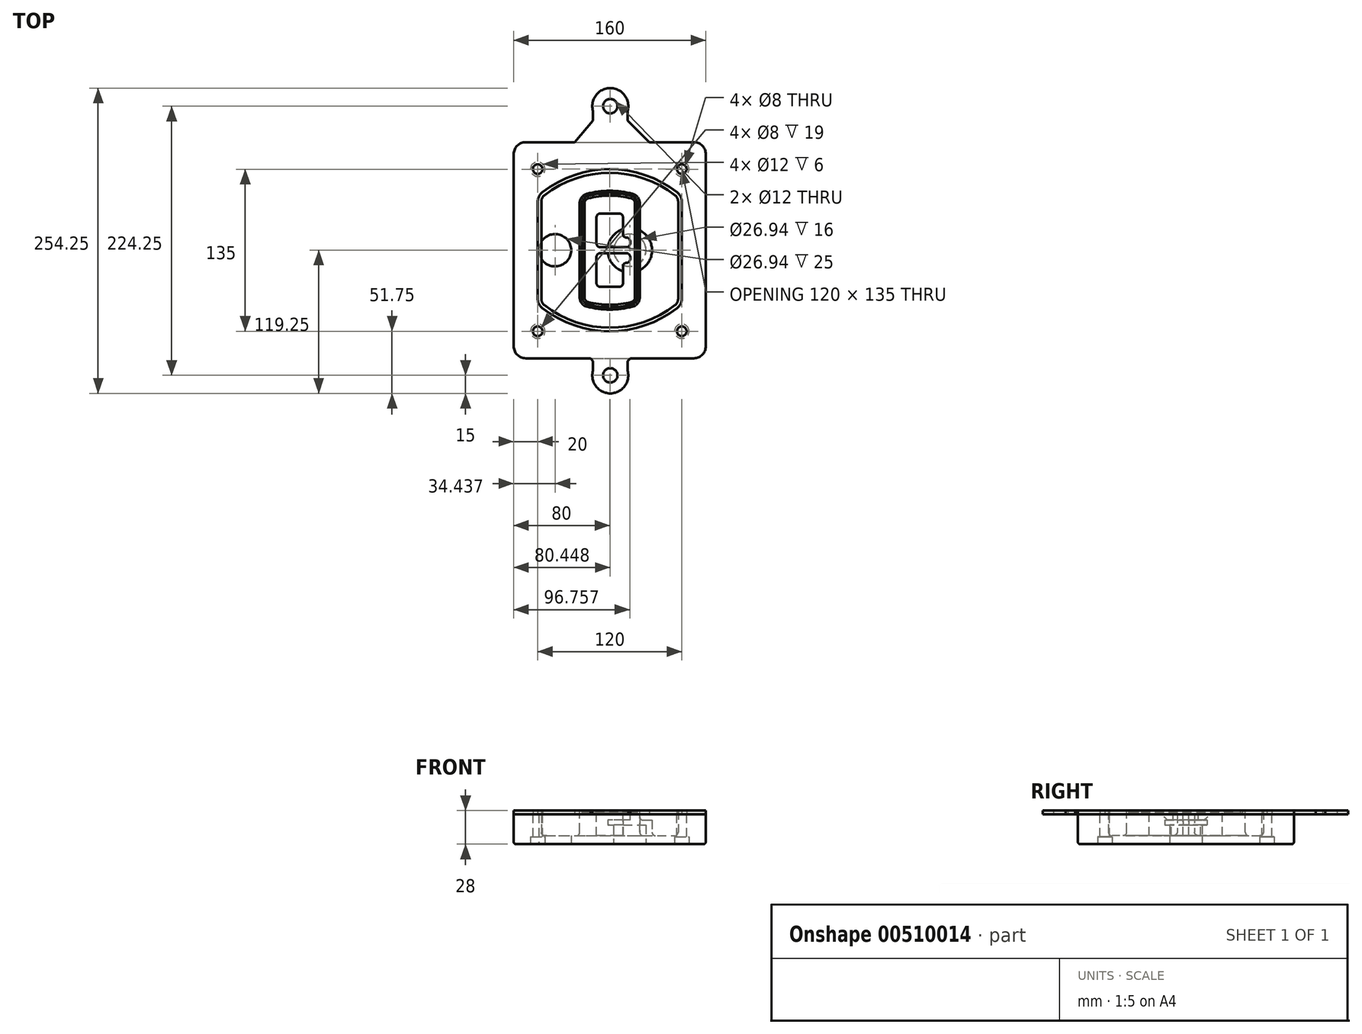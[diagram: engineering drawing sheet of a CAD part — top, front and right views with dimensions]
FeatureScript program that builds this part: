
annotation { "Feature Type Name" : "Feature", "Feature Type Description" : "" }
export const myFeature = defineFeature(function(context is Context, id is Id, definition is map)
    precondition{}
    {
        {
            var Q0;
            Q0=qCreatedBy(makeId("Top.planeOp"),FACE);
            var sketch = newSketch(context, id + "F0", { "sketchPlane" : qUnion([Q0])});
            skPoint(sketch, "E0.rect.middle", {"position": v(0, 0) * mm});
            skLineSegment(sketch, "E1.bottom", {"start": v(-70, -90) * mm, "end": v(70, -90) * mm});
            skLineSegment(sketch, "E1.top", {"start": v(-70, 90) * mm, "end": v(70, 90) * mm});
            skLineSegment(sketch, "E1.left", {"start": v(-80, -80) * mm, "end": v(-80, 80) * mm});
            skLineSegment(sketch, "E1.right", {"start": v(80, -80) * mm, "end": v(80, 80) * mm});
            skLineSegment(sketch, "E2", {"start": v(-80, 90) * mm, "end": v(80, -90) * mm, "construction": true});
            skLineSegment(sketch, "E3", {"start": v(80, 90) * mm, "end": v(-80, -90) * mm, "construction": true});
            skCircle(sketch, "E4", {"center": v(-60, 67.5) * mm, "radius": 4 * mm});
            skCircle(sketch, "E5", {"center": v(60, 67.5) * mm, "radius": 4 * mm});
            skCircle(sketch, "E6", {"center": v(60, -67.5) * mm, "radius": 4 * mm});
            skCircle(sketch, "E7", {"center": v(-60, -67.5) * mm, "radius": 4 * mm});
            skLineSegment(sketch, "E8", {"start": v(-60, 67.5) * mm, "end": v(60, 67.5) * mm, "construction": true});
            skLineSegment(sketch, "E9", {"start": v(60, 67.5) * mm, "end": v(60, -67.5) * mm, "construction": true});
            skLineSegment(sketch, "E10", {"start": v(60, -67.5) * mm, "end": v(-60, -67.5) * mm, "construction": true});
            skLineSegment(sketch, "E11", {"start": v(-60, -67.5) * mm, "end": v(-60, 67.5) * mm, "construction": true});
            skLineSegment(sketch, "E12", {"start": v(-60, 40.3) * mm, "end": v(-60, -40.3) * mm});
            skLineSegment(sketch, "E13", {"start": v(60, 40.3) * mm, "end": v(60, -40.3) * mm});
            skArc(sketch, "E14", {"start": v(56.15, 48.18) * mm, "mid": v(0, 67.5) * mm, "end": v(-56.15, 48.18) * mm});
            skArc(sketch, "E15", {"start": v(-56.15, -48.18) * mm, "mid": v(0, -67.5) * mm, "end": v(56.15, -48.18) * mm});
            skLineSegment(sketch, "E16", {"start": v(-60, 0) * mm, "end": v(60, 0) * mm, "construction": true});
            skPoint(sketch, "E17.visualSharp", {"position": v(-60, -45) * mm});
            skArc(sketch, "E17.filletArc", {"start": v(-60, -40.3) * mm, "mid": v(-58.99, -44.68) * mm, "end": v(-56.15, -48.18) * mm});
            skPoint(sketch, "E18.visualSharp", {"position": v(-60, 45) * mm});
            skArc(sketch, "E18.filletArc", {"start": v(-56.15, 48.18) * mm, "mid": v(-58.99, 44.68) * mm, "end": v(-60, 40.3) * mm});
            skPoint(sketch, "E19.visualSharp", {"position": v(60, 45) * mm});
            skArc(sketch, "E19.filletArc", {"start": v(60, 40.3) * mm, "mid": v(58.99, 44.68) * mm, "end": v(56.15, 48.18) * mm});
            skPoint(sketch, "E20.visualSharp", {"position": v(60, -45) * mm});
            skArc(sketch, "E20.filletArc", {"start": v(56.15, -48.18) * mm, "mid": v(58.99, -44.68) * mm, "end": v(60, -40.3) * mm});
            skPoint(sketch, "E21.visualSharp", {"position": v(-80, 90) * mm});
            skArc(sketch, "E21.filletArc", {"start": v(-70, 90) * mm, "mid": v(-77.07, 87.07) * mm, "end": v(-80, 80) * mm});
            skPoint(sketch, "E22.visualSharp", {"position": v(80, 90) * mm});
            skArc(sketch, "E22.filletArc", {"start": v(80, 80) * mm, "mid": v(77.07, 87.07) * mm, "end": v(70, 90) * mm});
            skPoint(sketch, "E23.visualSharp", {"position": v(80, -90) * mm});
            skArc(sketch, "E23.filletArc", {"start": v(70, -90) * mm, "mid": v(77.07, -87.07) * mm, "end": v(80, -80) * mm});
            skPoint(sketch, "E24.visualSharp", {"position": v(-80, -90) * mm});
            skArc(sketch, "E24.filletArc", {"start": v(-80, -80) * mm, "mid": v(-77.07, -87.07) * mm, "end": v(-70, -90) * mm});
            skArc(sketch, "E25.0", {"start": v(57, 40.3) * mm, "mid": v(56.3, 43.36) * mm, "end": v(54.3, 45.81) * mm});
            skLineSegment(sketch, "E25.1", {"start": v(57, 40.3) * mm, "end": v(57, -40.3) * mm});
            skArc(sketch, "E25.2", {"start": v(54.3, -45.81) * mm, "mid": v(56.3, -43.36) * mm, "end": v(57, -40.3) * mm});
            skArc(sketch, "E25.3", {"start": v(-54.3, -45.81) * mm, "mid": v(0, -64.5) * mm, "end": v(54.3, -45.81) * mm});
            skArc(sketch, "E25.4", {"start": v(-57, -40.3) * mm, "mid": v(-56.3, -43.36) * mm, "end": v(-54.3, -45.81) * mm});
            skArc(sketch, "E25.5", {"start": v(54.3, 45.81) * mm, "mid": v(0, 64.5) * mm, "end": v(-54.3, 45.81) * mm});
            skLineSegment(sketch, "E25.6", {"start": v(-57, 40.3) * mm, "end": v(-57, -40.3) * mm});
            skArc(sketch, "E25.7", {"start": v(-54.3, 45.81) * mm, "mid": v(-56.3, 43.36) * mm, "end": v(-57, 40.3) * mm});
            skArc(sketch, "E26.0", {"start": v(-58.62, 51.33) * mm, "mid": v(-62.58, 46.43) * mm, "end": v(-64, 40.3) * mm});
            skArc(sketch, "E26.1", {"start": v(58.62, 51.33) * mm, "mid": v(0, 71.5) * mm, "end": v(-58.62, 51.33) * mm});
            skArc(sketch, "E26.2", {"start": v(64, 40.3) * mm, "mid": v(62.58, 46.43) * mm, "end": v(58.62, 51.33) * mm});
            skLineSegment(sketch, "E26.3", {"start": v(64, 40.3) * mm, "end": v(64, -40.3) * mm});
            skArc(sketch, "E26.4", {"start": v(58.62, -51.33) * mm, "mid": v(62.58, -46.43) * mm, "end": v(64, -40.3) * mm});
            skLineSegment(sketch, "E26.5", {"start": v(-64, 40.3) * mm, "end": v(-64, -40.3) * mm});
            skArc(sketch, "E26.6", {"start": v(-58.62, -51.33) * mm, "mid": v(0, -71.5) * mm, "end": v(58.62, -51.33) * mm});
            skArc(sketch, "E26.7", {"start": v(-64, -40.3) * mm, "mid": v(-62.58, -46.43) * mm, "end": v(-58.62, -51.33) * mm});
            skSolve(sketch);
        }
        {
            var Q0;
            Q0=makeQuery(id+"F0.imprint","IMPRINT",FACE,{"disambiguationData":[TD([[makeQuery(id+"F0.imprint","IMPRINT",EDGE,{"derivedFrom":sQuery(id+"F0.wireOp",EDGE,"E1.bottom")}),1.0]])]});
            var Q1;
            Q1=makeQuery(id+"F0.imprint","IMPRINT",FACE,{"disambiguationData":[TD([[makeQuery(id+"F0.imprint","IMPRINT",EDGE,{"derivedFrom":sQuery(id+"F0.wireOp",EDGE,"E12")}),1.0]])]});
            var Q2;
            Q2=makeQuery(id+"F0.imprint","IMPRINT",FACE,{"disambiguationData":[TD([[makeQuery(id+"F0.imprint","IMPRINT",EDGE,{"derivedFrom":sQuery(id+"F0.wireOp",EDGE,"E25.0")}),1.0]])]});
            var Q3;
            Q3=makeQuery(id+"F0.imprint","IMPRINT",FACE,{"disambiguationData":[TD([[makeQuery(id+"F0.imprint","IMPRINT",EDGE,{"derivedFrom":sQuery(id+"F0.wireOp",EDGE,"E12")}),-1.0]])]});
            extrude(context, id + "F1", {"entities" : qUnion([Q0, Q1, Q2, Q3]), "oppositeDirection" : true, "depth" : 25 * mm});
        }
        {
            var Q0;
            Q0=makeQuery(id+"F0.imprint","IMPRINT",FACE,{"disambiguationData":[TD([[makeQuery(id+"F0.imprint","IMPRINT",EDGE,{"derivedFrom":sQuery(id+"F0.wireOp",EDGE,"E12")}),1.0]])]});
            extrude(context, id + "F2", {"entities" : qUnion([Q0]), "operationType" : NewBodyOperationType.ADD, "depth" : 3 * mm});
        }
        {
            var Q0;
            Q0=makeQuery(id+"F0.imprint","IMPRINT",FACE,{"disambiguationData":[TD([[makeQuery(id+"F0.imprint","IMPRINT",EDGE,{"derivedFrom":sQuery(id+"F0.wireOp",EDGE,"E25.0")}),1.0]])]});
            extrude(context, id + "F3", {"entities" : qUnion([Q0]), "operationType" : NewBodyOperationType.REMOVE, "oppositeDirection" : true, "depth" : 18 * mm});
        }
        {
            var Q0;
            Q0=makeQuery(id+"F2.opExtrude","CAP_FACE",FACE,{"disambiguationData":[OSD([sQuery(id+"F0.wireOp",EDGE,"E12"),sQuery(id+"F0.wireOp",EDGE,"E13"),sQuery(id+"F0.wireOp",EDGE,"E14"),sQuery(id+"F0.wireOp",EDGE,"E15"),sQuery(id+"F0.wireOp",EDGE,"E17.filletArc"),sQuery(id+"F0.wireOp",EDGE,"E18.filletArc"),sQuery(id+"F0.wireOp",EDGE,"E19.filletArc"),sQuery(id+"F0.wireOp",EDGE,"E20.filletArc"),sQuery(id+"F0.wireOp",EDGE,"E25.0"),sQuery(id+"F0.wireOp",EDGE,"E25.1"),sQuery(id+"F0.wireOp",EDGE,"E25.2"),sQuery(id+"F0.wireOp",EDGE,"E25.3"),sQuery(id+"F0.wireOp",EDGE,"E25.4"),sQuery(id+"F0.wireOp",EDGE,"E25.5"),sQuery(id+"F0.wireOp",EDGE,"E25.6"),sQuery(id+"F0.wireOp",EDGE,"E25.7")])],"isStart":false});
            var sketch = newSketch(context, id + "F4", { "sketchPlane" : qUnion([Q0])});
            skArc(sketch, "E27.0", {"start": v(-19.08, -46.97) * mm, "mid": v(0, -49.5) * mm, "end": v(19.08, -46.97) * mm});
            skArc(sketch, "E28.0", {"start": v(19.08, 46.97) * mm, "mid": v(0, 49.5) * mm, "end": v(-19.08, 46.97) * mm});
            skLineSegment(sketch, "E29", {"start": v(-25, 39.25) * mm, "end": v(-25, -39.25) * mm});
            skLineSegment(sketch, "E30", {"start": v(25, 39.25) * mm, "end": v(25, -39.25) * mm});
            skLineSegment(sketch, "E31", {"start": v(-25, 45.1) * mm, "end": v(25, 45.1) * mm, "construction": true});
            skLineSegment(sketch, "E32", {"start": v(-25, -45.1) * mm, "end": v(25, -45.1) * mm, "construction": true});
            skPoint(sketch, "E33.visualSharp", {"position": v(-25, 45.1) * mm});
            skArc(sketch, "E33.filletArc", {"start": v(-19.08, 46.97) * mm, "mid": v(-23.35, 44.11) * mm, "end": v(-25, 39.25) * mm});
            skPoint(sketch, "E34.visualSharp", {"position": v(25, 45.1) * mm});
            skArc(sketch, "E34.filletArc", {"start": v(25, 39.25) * mm, "mid": v(23.35, 44.11) * mm, "end": v(19.08, 46.97) * mm});
            skPoint(sketch, "E35.visualSharp", {"position": v(25, -45.1) * mm});
            skArc(sketch, "E35.filletArc", {"start": v(19.08, -46.97) * mm, "mid": v(23.35, -44.11) * mm, "end": v(25, -39.25) * mm});
            skPoint(sketch, "E36.visualSharp", {"position": v(-25, -45.1) * mm});
            skArc(sketch, "E36.filletArc", {"start": v(-25, -39.25) * mm, "mid": v(-23.35, -44.11) * mm, "end": v(-19.08, -46.97) * mm});
            skArc(sketch, "E37.0", {"start": v(54.3, 45.81) * mm, "mid": v(0, 64.5) * mm, "end": v(-54.3, 45.81) * mm});
            skArc(sketch, "E37.1", {"start": v(-54.3, 45.81) * mm, "mid": v(-56.3, 43.36) * mm, "end": v(-57, 40.3) * mm});
            skLineSegment(sketch, "E37.2", {"start": v(-57, 40.3) * mm, "end": v(-57, -40.3) * mm});
            skArc(sketch, "E37.3", {"start": v(-57, -40.3) * mm, "mid": v(-56.3, -43.36) * mm, "end": v(-54.3, -45.81) * mm});
            skArc(sketch, "E37.4", {"start": v(-54.3, -45.81) * mm, "mid": v(0, -64.5) * mm, "end": v(54.3, -45.81) * mm});
            skArc(sketch, "E37.5", {"start": v(54.3, -45.81) * mm, "mid": v(56.3, -43.36) * mm, "end": v(57, -40.3) * mm});
            skLineSegment(sketch, "E37.6", {"start": v(57, 40.3) * mm, "end": v(57, -40.3) * mm});
            skArc(sketch, "E37.7", {"start": v(57, 40.3) * mm, "mid": v(56.3, 43.36) * mm, "end": v(54.3, 45.81) * mm});
            skLineSegment(sketch, "E38.0", {"start": v(23, 39.25) * mm, "end": v(23, -39.25) * mm});
            skArc(sketch, "E38.1", {"start": v(18.56, -45.04) * mm, "mid": v(21.76, -42.9) * mm, "end": v(23, -39.25) * mm});
            skArc(sketch, "E38.2", {"start": v(-18.56, -45.04) * mm, "mid": v(0, -47.5) * mm, "end": v(18.56, -45.04) * mm});
            skArc(sketch, "E38.3", {"start": v(-23, -39.25) * mm, "mid": v(-21.76, -42.9) * mm, "end": v(-18.56, -45.04) * mm});
            skLineSegment(sketch, "E38.4", {"start": v(-23, 39.25) * mm, "end": v(-23, -39.25) * mm});
            skArc(sketch, "E38.5", {"start": v(23, 39.25) * mm, "mid": v(21.76, 42.9) * mm, "end": v(18.56, 45.04) * mm});
            skArc(sketch, "E38.6", {"start": v(-18.56, 45.04) * mm, "mid": v(-21.76, 42.9) * mm, "end": v(-23, 39.25) * mm});
            skArc(sketch, "E38.7", {"start": v(18.56, 45.04) * mm, "mid": v(0, 47.5) * mm, "end": v(-18.56, 45.04) * mm});
            skArc(sketch, "E39.0", {"start": v(21, 39.25) * mm, "mid": v(20.18, 41.68) * mm, "end": v(18.04, 43.1) * mm});
            skLineSegment(sketch, "E39.1", {"start": v(21, 39.25) * mm, "end": v(21, -39.25) * mm});
            skArc(sketch, "E39.2", {"start": v(18.04, -43.1) * mm, "mid": v(20.18, -41.68) * mm, "end": v(21, -39.25) * mm});
            skArc(sketch, "E39.3", {"start": v(-18.04, -43.1) * mm, "mid": v(0, -45.5) * mm, "end": v(18.04, -43.1) * mm});
            skArc(sketch, "E39.4", {"start": v(-21, -39.25) * mm, "mid": v(-20.18, -41.68) * mm, "end": v(-18.04, -43.1) * mm});
            skArc(sketch, "E39.5", {"start": v(18.04, 43.1) * mm, "mid": v(0, 45.5) * mm, "end": v(-18.04, 43.1) * mm});
            skLineSegment(sketch, "E39.6", {"start": v(-21, 39.25) * mm, "end": v(-21, -39.25) * mm});
            skArc(sketch, "E39.7", {"start": v(-18.04, 43.1) * mm, "mid": v(-20.18, 41.68) * mm, "end": v(-21, 39.25) * mm});
            skLineSegment(sketch, "E40", {"start": v(-25, 0) * mm, "end": v(25, 0) * mm, "construction": true});
            skLineSegment(sketch, "E41", {"start": v(-11, 5.5) * mm, "end": v(-11, 27.5) * mm});
            skLineSegment(sketch, "E42", {"start": v(-8, 30.5) * mm, "end": v(8, 30.5) * mm});
            skLineSegment(sketch, "E43", {"start": v(11, 27.5) * mm, "end": v(11, 13.5) * mm});
            skLineSegment(sketch, "E44", {"start": v(14, 10.5) * mm, "end": v(14, 10.5) * mm});
            skLineSegment(sketch, "E45", {"start": v(17, 7.5) * mm, "end": v(17, 5.5) * mm});
            skLineSegment(sketch, "E46", {"start": v(14, 2.5) * mm, "end": v(-8, 2.5) * mm});
            skPoint(sketch, "E47.visualSharp", {"position": v(-11, 30.5) * mm});
            skArc(sketch, "E47.filletArc", {"start": v(-8, 30.5) * mm, "mid": v(-10.12, 29.62) * mm, "end": v(-11, 27.5) * mm});
            skPoint(sketch, "E48.visualSharp", {"position": v(11, 30.5) * mm});
            skArc(sketch, "E48.filletArc", {"start": v(11, 27.5) * mm, "mid": v(10.12, 29.62) * mm, "end": v(8, 30.5) * mm});
            skPoint(sketch, "E49.visualSharp", {"position": v(11, 10.5) * mm});
            skArc(sketch, "E49.filletArc", {"start": v(11, 13.5) * mm, "mid": v(11.88, 11.38) * mm, "end": v(14, 10.5) * mm});
            skPoint(sketch, "E50.visualSharp", {"position": v(17, 10.5) * mm});
            skArc(sketch, "E50.filletArc", {"start": v(17, 7.5) * mm, "mid": v(16.12, 9.62) * mm, "end": v(14, 10.5) * mm});
            skPoint(sketch, "E51.visualSharp", {"position": v(17, 2.5) * mm});
            skArc(sketch, "E51.filletArc", {"start": v(14, 2.5) * mm, "mid": v(16.12, 3.38) * mm, "end": v(17, 5.5) * mm});
            skPoint(sketch, "E52.visualSharp", {"position": v(-11, 2.5) * mm});
            skArc(sketch, "E52.filletArc", {"start": v(-11, 5.5) * mm, "mid": v(-10.12, 3.38) * mm, "end": v(-8, 2.5) * mm});
            skLineSegment(sketch, "E53.0.MirrorCS", {"start": v(14, -2.5) * mm, "end": v(-8, -2.5) * mm});
            skArc(sketch, "E54.0.MirrorCS", {"start": v(-11, -5.5) * mm, "mid": v(-10.12, -3.38) * mm, "end": v(-8, -2.5) * mm});
            skLineSegment(sketch, "E55.0.MirrorCS", {"start": v(-11, -5.5) * mm, "end": v(-11, -27.5) * mm});
            skArc(sketch, "E56.0.MirrorCS", {"start": v(-8, -30.5) * mm, "mid": v(-10.12, -29.62) * mm, "end": v(-11, -27.5) * mm});
            skLineSegment(sketch, "E57.0.MirrorCS", {"start": v(-8, -30.5) * mm, "end": v(8, -30.5) * mm});
            skArc(sketch, "E58.0.MirrorCS", {"start": v(11, -27.5) * mm, "mid": v(10.12, -29.62) * mm, "end": v(8, -30.5) * mm});
            skLineSegment(sketch, "E59.0.MirrorCS", {"start": v(11, -27.5) * mm, "end": v(11, -13.5) * mm});
            skArc(sketch, "E60.0.MirrorCS", {"start": v(11, -13.5) * mm, "mid": v(11.88, -11.38) * mm, "end": v(14, -10.5) * mm});
            skArc(sketch, "E61.0.MirrorCS", {"start": v(17, -7.5) * mm, "mid": v(16.12, -9.62) * mm, "end": v(14, -10.5) * mm});
            skLineSegment(sketch, "E62.0.MirrorCS", {"start": v(17, -7.5) * mm, "end": v(17, -5.5) * mm});
            skArc(sketch, "E63.0.MirrorCS", {"start": v(14, -2.5) * mm, "mid": v(16.12, -3.38) * mm, "end": v(17, -5.5) * mm});
            skSolve(sketch);
        }
        {
            var Q0;
            Q0=makeQuery(id+"F4.imprint","IMPRINT",FACE,{"disambiguationData":[TD([[makeQuery(id+"F4.imprint","IMPRINT",EDGE,{"derivedFrom":sQuery(id+"F4.wireOp",EDGE,"E27.0")}),1.0]])]});
            var Q1;
            Q1=makeQuery(id+"F4.imprint","IMPRINT",FACE,{"disambiguationData":[TD([[makeQuery(id+"F4.imprint","IMPRINT",EDGE,{"derivedFrom":sQuery(id+"F4.wireOp",EDGE,"E38.0")}),-1.0]])]});
            var Q2;
            Q2=makeQuery(id+"F4.imprint","IMPRINT",FACE,{"disambiguationData":[TD([[makeQuery(id+"F4.imprint","IMPRINT",EDGE,{"derivedFrom":sQuery(id+"F4.wireOp",EDGE,"E39.0")}),1.0]])]});
            extrude(context, id + "F5", {"entities" : qUnion([Q0, Q1, Q2]), "operationType" : NewBodyOperationType.ADD, "endBound" : BoundingType.UP_TO_NEXT, "oppositeDirection" : true, "depth" : 25 * mm});
        }
        {
            var Q0;
            Q0=makeQuery(id+"F4.imprint","IMPRINT",FACE,{"disambiguationData":[TD([[makeQuery(id+"F4.imprint","IMPRINT",EDGE,{"derivedFrom":sQuery(id+"F4.wireOp",EDGE,"E38.0")}),-1.0]])]});
            extrude(context, id + "F6", {"entities" : qUnion([Q0]), "operationType" : NewBodyOperationType.REMOVE, "oppositeDirection" : true, "depth" : 2 * mm});
        }
        {
            var Q0;
            Q0=makeQuery(id+"F1.opExtrude","CAP_FACE",FACE,{"disambiguationData":[OSD([sQuery(id+"F0.wireOp",EDGE,"E1.bottom"),sQuery(id+"F0.wireOp",EDGE,"E1.top"),sQuery(id+"F0.wireOp",EDGE,"E1.left"),sQuery(id+"F0.wireOp",EDGE,"E1.right"),sQuery(id+"F0.wireOp",EDGE,"E4"),sQuery(id+"F0.wireOp",EDGE,"E5"),sQuery(id+"F0.wireOp",EDGE,"E6"),sQuery(id+"F0.wireOp",EDGE,"E7"),sQuery(id+"F0.wireOp",EDGE,"E21.filletArc"),sQuery(id+"F0.wireOp",EDGE,"E22.filletArc"),sQuery(id+"F0.wireOp",EDGE,"E23.filletArc"),sQuery(id+"F0.wireOp",EDGE,"E24.filletArc")])],"isStart":false});
            var sketch = newSketch(context, id + "F7", { "sketchPlane" : qUnion([Q0])});
            skCircle(sketch, "E64", {"center": v(16.76, 0) * mm, "radius": 13.47 * mm});
            skCircle(sketch, "E65", {"center": v(-45.56, 0) * mm, "radius": 13.47 * mm});
            skLineSegment(sketch, "E66", {"start": v(80, 0) * mm, "end": v(-80, 0) * mm});
            skCircle(sketch, "E67", {"center": v(16.76, 0) * mm, "radius": 18.47 * mm});
            skCircle(sketch, "E68", {"center": v(60, -67.5) * mm, "radius": 6 * mm});
            skCircle(sketch, "E69", {"center": v(-60, -67.5) * mm, "radius": 6 * mm});
            skCircle(sketch, "E70", {"center": v(-60, 67.5) * mm, "radius": 6 * mm});
            skCircle(sketch, "E71", {"center": v(60, 67.5) * mm, "radius": 6 * mm});
            skSolve(sketch);
        }
        {
            var Q0;
            {var subQ1=sQuery(id+"F7.wireOp",EDGE,"E66");var subQ4=sQuery(id+"F7.wireOp",EDGE,"E64");var subQ6=makeQuery(id+"F7.imprint","INTERSECT",VERTEX,{"disambiguationData":[OD(0.0)],"derivedFrom":[subQ4,subQ1]});Q0=makeQuery(id+"F7.imprint","IMPRINT",FACE,{"disambiguationData":[TD([[makeQuery(id+"F7.imprint","IMPRINT",EDGE,{"disambiguationData":[TD([[subQ6,-1.0]])],"derivedFrom":subQ4}),-1.0]])]});}
            var Q1;
            {var subQ0=sQuery(id+"F7.wireOp",EDGE,"E66");var subQ1=sQuery(id+"F7.wireOp",EDGE,"E64");var subQ3=makeQuery(id+"F7.imprint","INTERSECT",VERTEX,{"disambiguationData":[OD(0.0)],"derivedFrom":[subQ1,subQ0]});Q1=makeQuery(id+"F7.imprint","IMPRINT",FACE,{"disambiguationData":[TD([[makeQuery(id+"F7.imprint","IMPRINT",EDGE,{"disambiguationData":[TD([[subQ3,-1.0]])],"derivedFrom":subQ1}),1.0]])]});}
            var Q2;
            {var subQ0=sQuery(id+"F7.wireOp",EDGE,"E66");var subQ1=sQuery(id+"F7.wireOp",EDGE,"E64");var subQ3=makeQuery(id+"F7.imprint","INTERSECT",VERTEX,{"disambiguationData":[OD(0.0)],"derivedFrom":[subQ1,subQ0]});Q2=makeQuery(id+"F7.imprint","IMPRINT",FACE,{"disambiguationData":[TD([[makeQuery(id+"F7.imprint","IMPRINT",EDGE,{"disambiguationData":[TD([[subQ3,1.0]])],"derivedFrom":subQ1}),1.0]])]});}
            var Q3;
            {var subQ1=sQuery(id+"F7.wireOp",EDGE,"E66");var subQ4=sQuery(id+"F7.wireOp",EDGE,"E64");var subQ6=makeQuery(id+"F7.imprint","INTERSECT",VERTEX,{"disambiguationData":[OD(0.0)],"derivedFrom":[subQ4,subQ1]});Q3=makeQuery(id+"F7.imprint","IMPRINT",FACE,{"disambiguationData":[TD([[makeQuery(id+"F7.imprint","IMPRINT",EDGE,{"disambiguationData":[TD([[subQ6,1.0]])],"derivedFrom":subQ4}),-1.0]])]});}
            extrude(context, id + "F8", {"entities" : qUnion([Q0, Q1, Q2, Q3]), "operationType" : NewBodyOperationType.ADD, "oppositeDirection" : true, "depth" : 20 * mm});
        }
        {
            var Q0;
            {var subQ0=sQuery(id+"F7.wireOp",EDGE,"E66");var subQ1=sQuery(id+"F7.wireOp",EDGE,"E64");var subQ3=makeQuery(id+"F7.imprint","INTERSECT",VERTEX,{"disambiguationData":[OD(0.0)],"derivedFrom":[subQ1,subQ0]});Q0=makeQuery(id+"F7.imprint","IMPRINT",FACE,{"disambiguationData":[TD([[makeQuery(id+"F7.imprint","IMPRINT",EDGE,{"disambiguationData":[TD([[subQ3,-1.0]])],"derivedFrom":subQ1}),1.0]])]});}
            var Q1;
            {var subQ0=sQuery(id+"F7.wireOp",EDGE,"E66");var subQ1=sQuery(id+"F7.wireOp",EDGE,"E64");var subQ3=makeQuery(id+"F7.imprint","INTERSECT",VERTEX,{"disambiguationData":[OD(0.0)],"derivedFrom":[subQ1,subQ0]});Q1=makeQuery(id+"F7.imprint","IMPRINT",FACE,{"disambiguationData":[TD([[makeQuery(id+"F7.imprint","IMPRINT",EDGE,{"disambiguationData":[TD([[subQ3,1.0]])],"derivedFrom":subQ1}),1.0]])]});}
            extrude(context, id + "F9", {"entities" : qUnion([Q0, Q1]), "operationType" : NewBodyOperationType.REMOVE, "oppositeDirection" : true, "depth" : 16 * mm});
        }
        {
            var Q0;
            {var subQ0=sQuery(id+"F7.wireOp",EDGE,"E66");var subQ1=sQuery(id+"F7.wireOp",EDGE,"E65");var subQ3=makeQuery(id+"F7.imprint","INTERSECT",VERTEX,{"disambiguationData":[OD(0.0)],"derivedFrom":[subQ1,subQ0]});Q0=makeQuery(id+"F7.imprint","IMPRINT",FACE,{"disambiguationData":[TD([[makeQuery(id+"F7.imprint","IMPRINT",EDGE,{"disambiguationData":[TD([[subQ3,-1.0]])],"derivedFrom":subQ1}),1.0]])]});}
            var Q1;
            {var subQ0=sQuery(id+"F7.wireOp",EDGE,"E66");var subQ1=sQuery(id+"F7.wireOp",EDGE,"E65");var subQ3=makeQuery(id+"F7.imprint","INTERSECT",VERTEX,{"disambiguationData":[OD(0.0)],"derivedFrom":[subQ1,subQ0]});Q1=makeQuery(id+"F7.imprint","IMPRINT",FACE,{"disambiguationData":[TD([[makeQuery(id+"F7.imprint","IMPRINT",EDGE,{"disambiguationData":[TD([[subQ3,1.0]])],"derivedFrom":subQ1}),1.0]])]});}
            extrude(context, id + "F10", {"entities" : qUnion([Q0, Q1]), "operationType" : NewBodyOperationType.REMOVE, "oppositeDirection" : true, "depth" : 25 * mm});
        }
        {
            var Q0;
            Q0=makeQuery(id+"F7.imprint","IMPRINT",FACE,{"disambiguationData":[TD([[makeQuery(id+"F7.imprint","IMPRINT",EDGE,{"derivedFrom":sQuery(id+"F7.wireOp",EDGE,"E68")}),1.0]])]});
            var Q1;
            Q1=makeQuery(id+"F7.imprint","IMPRINT",FACE,{"disambiguationData":[TD([[makeQuery(id+"F7.imprint","IMPRINT",EDGE,{"derivedFrom":makeQuery(id+"F1.opExtrude","CAP_EDGE",EDGE,{"disambiguationData":[OSD([sQuery(id+"F0.wireOp",EDGE,"E5")])],"isStart":false})}),-1.0]])]});
            var Q2;
            Q2=makeQuery(id+"F7.imprint","IMPRINT",FACE,{"disambiguationData":[TD([[makeQuery(id+"F7.imprint","IMPRINT",EDGE,{"derivedFrom":sQuery(id+"F7.wireOp",EDGE,"E69")}),1.0]])]});
            var Q3;
            Q3=makeQuery(id+"F7.imprint","IMPRINT",FACE,{"disambiguationData":[TD([[makeQuery(id+"F7.imprint","IMPRINT",EDGE,{"derivedFrom":makeQuery(id+"F1.opExtrude","CAP_EDGE",EDGE,{"disambiguationData":[OSD([sQuery(id+"F0.wireOp",EDGE,"E4")])],"isStart":false})}),-1.0]])]});
            var Q4;
            Q4=makeQuery(id+"F7.imprint","IMPRINT",FACE,{"disambiguationData":[TD([[makeQuery(id+"F7.imprint","IMPRINT",EDGE,{"derivedFrom":sQuery(id+"F7.wireOp",EDGE,"E70")}),1.0]])]});
            var Q5;
            Q5=makeQuery(id+"F7.imprint","IMPRINT",FACE,{"disambiguationData":[TD([[makeQuery(id+"F7.imprint","IMPRINT",EDGE,{"derivedFrom":makeQuery(id+"F1.opExtrude","CAP_EDGE",EDGE,{"disambiguationData":[OSD([sQuery(id+"F0.wireOp",EDGE,"E7")])],"isStart":false})}),-1.0]])]});
            var Q6;
            Q6=makeQuery(id+"F7.imprint","IMPRINT",FACE,{"disambiguationData":[TD([[makeQuery(id+"F7.imprint","IMPRINT",EDGE,{"derivedFrom":sQuery(id+"F7.wireOp",EDGE,"E71")}),1.0]])]});
            var Q7;
            Q7=makeQuery(id+"F7.imprint","IMPRINT",FACE,{"disambiguationData":[TD([[makeQuery(id+"F7.imprint","IMPRINT",EDGE,{"derivedFrom":makeQuery(id+"F1.opExtrude","CAP_EDGE",EDGE,{"disambiguationData":[OSD([sQuery(id+"F0.wireOp",EDGE,"E6")])],"isStart":false})}),-1.0]])]});
            extrude(context, id + "F11", {"entities" : qUnion([Q0, Q1, Q2, Q3, Q4, Q5, Q6, Q7]), "operationType" : NewBodyOperationType.REMOVE, "oppositeDirection" : true, "depth" : 6 * mm});
        }
        {
            var Q0;
            Q0=makeQuery(id+"F9.boolean.opBoolean","COPY",FACE,{"derivedFrom":makeQuery(id+"F9.opExtrude","CAP_FACE",FACE,{"disambiguationData":[OSD([sQuery(id+"F7.wireOp",EDGE,"E64")])],"isStart":false})});
            var sketch = newSketch(context, id + "F12", { "sketchPlane" : qUnion([Q0])});
            skArc(sketch, "E72.0", {"start": v(11, 17.55) * mm, "mid": v(2.57, 11.82) * mm, "end": v(-1.54, 2.5) * mm});
            skArc(sketch, "E72.1", {"start": v(-1.54, -2.5) * mm, "mid": v(2.57, -11.82) * mm, "end": v(11, -17.55) * mm});
            skLineSegment(sketch, "E73", {"start": v(-1.54, -2.5) * mm, "end": v(14, -2.5) * mm});
            skLineSegment(sketch, "E74.0", {"start": v(14, 2.5) * mm, "end": v(-1.54, 2.5) * mm});
            skArc(sketch, "E74.1", {"start": v(14, 2.5) * mm, "mid": v(16.12, 3.38) * mm, "end": v(17, 5.5) * mm});
            skLineSegment(sketch, "E74.2", {"start": v(17, 7.5) * mm, "end": v(17, 5.5) * mm});
            skArc(sketch, "E74.3", {"start": v(17, 7.5) * mm, "mid": v(16.12, 9.62) * mm, "end": v(14, 10.5) * mm});
            skArc(sketch, "E74.4", {"start": v(11, 13.5) * mm, "mid": v(11.88, 11.38) * mm, "end": v(14, 10.5) * mm});
            skLineSegment(sketch, "E74.5", {"start": v(11, 17.55) * mm, "end": v(11, 13.5) * mm});
            skLineSegment(sketch, "E74.7", {"start": v(14, -2.5) * mm, "end": v(-1.54, -2.5) * mm});
            skArc(sketch, "E74.8", {"start": v(14, -2.5) * mm, "mid": v(16.12, -3.38) * mm, "end": v(17, -5.5) * mm});
            skLineSegment(sketch, "E74.9", {"start": v(17, -7.5) * mm, "end": v(17, -5.5) * mm});
            skArc(sketch, "E74.10", {"start": v(17, -7.5) * mm, "mid": v(16.12, -9.62) * mm, "end": v(14, -10.5) * mm});
            skArc(sketch, "E74.11", {"start": v(11, -13.5) * mm, "mid": v(11.88, -11.38) * mm, "end": v(14, -10.5) * mm});
            skLineSegment(sketch, "E74.12", {"start": v(11, -17.55) * mm, "end": v(11, -13.5) * mm});
            skPoint(sketch, "E75.orphan", {"position": v(11, -27.5) * mm});
            skPoint(sketch, "E76.orphan", {"position": v(-8, -2.5) * mm});
            skPoint(sketch, "E77.orphan", {"position": v(-8, 2.5) * mm});
            skPoint(sketch, "E78.orphan", {"position": v(11, 27.5) * mm});
            skSolve(sketch);
        }
        {
            var Q0;
            {var subQ7=sQuery(id+"F12.wireOp",EDGE,"E72.0");var subQ14=sQuery(id+"F12.wireOp",EDGE,"E72.1");var subQ16=sQuery(id+"F12.wireOp",EDGE,"E74.1");var subQ18=sQuery(id+"F12.wireOp",EDGE,"E74.8");Q0=qUnion([makeQuery(id+"F12.imprint","IMPRINT",FACE,{"disambiguationData":[TD([[makeQuery(id+"F12.imprint","IMPRINT",EDGE,{"derivedFrom":subQ7}),1.0]])]}),makeQuery(id+"F12.imprint","IMPRINT",FACE,{"disambiguationData":[TD([[makeQuery(id+"F12.imprint","IMPRINT",EDGE,{"derivedFrom":subQ14}),1.0]])]}),makeQuery(id+"F12.imprint","IMPRINT",FACE,{"disambiguationData":[TD([[makeQuery(id+"F12.imprint","IMPRINT",EDGE,{"derivedFrom":subQ16}),1.0]])]}),makeQuery(id+"F12.imprint","IMPRINT",FACE,{"disambiguationData":[TD([[makeQuery(id+"F12.imprint","IMPRINT",EDGE,{"derivedFrom":subQ18}),-1.0]])]})]);}
            var Q1;
            Q1=makeQuery(id+"F5.boolean.opBoolean","SPLIT",FACE,{"disambiguationData":[TD([makeQuery(id+"F5.opExtrude","SWEPT_FACE",FACE,{"disambiguationData":[OSD([sQuery(id+"F4.wireOp",EDGE,"E41")])]})])],"derivedFrom":makeQuery(id+"F3.boolean.opBoolean","COPY",FACE,{"derivedFrom":makeQuery(id+"F3.opExtrude","CAP_FACE",FACE,{"disambiguationData":[OSD([sQuery(id+"F0.wireOp",EDGE,"E25.0"),sQuery(id+"F0.wireOp",EDGE,"E25.1"),sQuery(id+"F0.wireOp",EDGE,"E25.2"),sQuery(id+"F0.wireOp",EDGE,"E25.3"),sQuery(id+"F0.wireOp",EDGE,"E25.4"),sQuery(id+"F0.wireOp",EDGE,"E25.5"),sQuery(id+"F0.wireOp",EDGE,"E25.6"),sQuery(id+"F0.wireOp",EDGE,"E25.7")])],"isStart":false})})});
            extrude(context, id + "F13", {"entities" : qUnion([Q0]), "operationType" : NewBodyOperationType.REMOVE, "endBound" : BoundingType.UP_TO_SURFACE, "endBoundEntityFace" : qUnion([Q1]), "depth" : 25 * mm});
        }
        {
            var Q0;
            Q0=makeQuery(id+"F3.boolean.opBoolean","COPY",EDGE,{"derivedFrom":makeQuery(id+"F3.opExtrude","CAP_EDGE",EDGE,{"disambiguationData":[OSD([sQuery(id+"F0.wireOp",EDGE,"E25.6")])],"isStart":false})});
            var Q1;
            Q1=makeQuery(id+"F8.boolean.opBoolean","INTERSECT",EDGE,{"derivedFrom":[makeQuery(id+"F5.opExtrude","SWEPT_FACE",FACE,{"disambiguationData":[OSD([sQuery(id+"F4.wireOp",EDGE,"E30")])]}),makeQuery(id+"F8.opExtrude","CAP_FACE",FACE,{"disambiguationData":[OSD([sQuery(id+"F7.wireOp",EDGE,"E67")])],"isStart":false})]});
            var Q2;
            Q2=makeQuery(id+"F8.boolean.opBoolean","INTERSECT",EDGE,{"disambiguationData":[OD(1.0)],"derivedFrom":[makeQuery(id+"F5.opExtrude","SWEPT_FACE",FACE,{"disambiguationData":[OSD([sQuery(id+"F4.wireOp",EDGE,"E30")])]}),makeQuery(id+"F8.opExtrude","SWEPT_FACE",FACE,{"disambiguationData":[OSD([sQuery(id+"F7.wireOp",EDGE,"E67")])]})]});
            var Q3;
            {var subQ0=sQuery(id+"F4.wireOp",EDGE,"E30");Q3=makeQuery(id+"F8.boolean.opBoolean","SPLIT",EDGE,{"disambiguationData":[TD([makeQuery(id+"F5.opExtrude","SWEPT_FACE",FACE,{"disambiguationData":[OSD([sQuery(id+"F4.wireOp",EDGE,"E35.filletArc")])]})])],"derivedFrom":makeQuery(id+"F5.opExtrude","CAP_EDGE",EDGE,{"disambiguationData":[OSD([subQ0])],"isStart":false})});}
            var Q4;
            {var subQ0=sQuery(id+"F0.wireOp",EDGE,"E25.7");var subQ1=sQuery(id+"F0.wireOp",EDGE,"E25.1");var subQ2=sQuery(id+"F0.wireOp",EDGE,"E25.6");var subQ3=sQuery(id+"F0.wireOp",EDGE,"E25.5");var subQ4=sQuery(id+"F0.wireOp",EDGE,"E25.4");var subQ5=sQuery(id+"F0.wireOp",EDGE,"E25.0");var subQ6=sQuery(id+"F0.wireOp",EDGE,"E25.2");var subQ7=sQuery(id+"F0.wireOp",EDGE,"E25.3");Q4=makeQuery(id+"F8.boolean.opBoolean","INTERSECT",EDGE,{"derivedFrom":[makeQuery(id+"F5.boolean.opBoolean","SPLIT",FACE,{"disambiguationData":[TD([makeQuery(id+"F2.opExtrude","SWEPT_FACE",FACE,{"disambiguationData":[OSD([subQ5])]})])],"derivedFrom":makeQuery(id+"F3.boolean.opBoolean","COPY",FACE,{"derivedFrom":makeQuery(id+"F3.opExtrude","CAP_FACE",FACE,{"disambiguationData":[OSD([subQ5,subQ1,subQ6,subQ7,subQ4,subQ3,subQ2,subQ0])],"isStart":false})})}),makeQuery(id+"F8.opExtrude","SWEPT_FACE",FACE,{"disambiguationData":[OSD([sQuery(id+"F7.wireOp",EDGE,"E67")])]})]});}
            var Q5;
            Q5=makeQuery(id+"F8.boolean.opBoolean","INTERSECT",EDGE,{"disambiguationData":[OD(0.0)],"derivedFrom":[makeQuery(id+"F5.opExtrude","SWEPT_FACE",FACE,{"disambiguationData":[OSD([sQuery(id+"F4.wireOp",EDGE,"E30")])]}),makeQuery(id+"F8.opExtrude","SWEPT_FACE",FACE,{"disambiguationData":[OSD([sQuery(id+"F7.wireOp",EDGE,"E67")])]})]});
            fillet(context, id + "F14", {"entities" : qUnion([Q0, Q1, Q2, Q3, Q4, Q5]), "radius" : 3 * mm, "tangentPropagation" : true, "allowEdgeOverflow" : false});
        }
        {
            var Q0;
            Q0=makeQuery(id+"F1.opExtrude","CAP_EDGE",EDGE,{"disambiguationData":[OSD([sQuery(id+"F0.wireOp",EDGE,"E1.bottom")])],"isStart":false});
            fillet(context, id + "F15", {"entities" : qUnion([Q0]), "radius" : 2 * mm, "tangentPropagation" : true, "allowEdgeOverflow" : false});
        }
        {
            var Q0;
            {var subQ0=sQuery(id+"F0.wireOp",EDGE,"E21.filletArc");var subQ1=sQuery(id+"F0.wireOp",EDGE,"E7");var subQ2=sQuery(id+"F0.wireOp",EDGE,"E6");var subQ3=sQuery(id+"F0.wireOp",EDGE,"E5");var subQ4=sQuery(id+"F0.wireOp",EDGE,"E4");var subQ5=sQuery(id+"F0.wireOp",EDGE,"E22.filletArc");var subQ6=sQuery(id+"F0.wireOp",EDGE,"E1.bottom");var subQ7=sQuery(id+"F0.wireOp",EDGE,"E1.right");var subQ8=sQuery(id+"F0.wireOp",EDGE,"E1.top");var subQ9=sQuery(id+"F0.wireOp",EDGE,"E1.left");var subQ10=sQuery(id+"F0.wireOp",EDGE,"E23.filletArc");var subQ11=sQuery(id+"F0.wireOp",EDGE,"E24.filletArc");Q0=makeQuery(id+"F2.boolean.opBoolean","SPLIT",FACE,{"disambiguationData":[TD([makeQuery(id+"F1.opExtrude","SWEPT_FACE",FACE,{"disambiguationData":[OSD([subQ6])]})])],"derivedFrom":makeQuery(id+"F1.opExtrude","CAP_FACE",FACE,{"disambiguationData":[OSD([subQ6,subQ8,subQ9,subQ7,subQ4,subQ3,subQ2,subQ1,subQ0,subQ5,subQ10,subQ11])],"isStart":true})});}
            var sketch = newSketch(context, id + "F16", { "sketchPlane" : qUnion([Q0])});
            skArc(sketch, "E79.0", {"start": v(56.15, 48.18) * mm, "mid": v(0, 67.5) * mm, "end": v(-56.15, 48.18) * mm});
            skArc(sketch, "E79.1", {"start": v(-56.15, 48.18) * mm, "mid": v(-58.99, 44.68) * mm, "end": v(-60, 40.3) * mm});
            skLineSegment(sketch, "E79.2", {"start": v(-60, 40.3) * mm, "end": v(-60, -40.3) * mm});
            skArc(sketch, "E79.3", {"start": v(-60, -40.3) * mm, "mid": v(-58.99, -44.68) * mm, "end": v(-56.15, -48.18) * mm});
            skArc(sketch, "E79.4", {"start": v(-56.15, -48.18) * mm, "mid": v(0, -67.5) * mm, "end": v(56.15, -48.18) * mm});
            skArc(sketch, "E79.5", {"start": v(56.15, -48.18) * mm, "mid": v(58.99, -44.68) * mm, "end": v(60, -40.3) * mm});
            skLineSegment(sketch, "E79.6", {"start": v(60, 40.3) * mm, "end": v(60, -40.3) * mm});
            skArc(sketch, "E79.7", {"start": v(60, 40.3) * mm, "mid": v(58.99, 44.68) * mm, "end": v(56.15, 48.18) * mm});
            skCircle(sketch, "E80.0", {"center": v(60, 67.5) * mm, "radius": 4 * mm});
            skCircle(sketch, "E80.1", {"center": v(-60, 67.5) * mm, "radius": 4 * mm});
            skCircle(sketch, "E80.2", {"center": v(-60, -67.5) * mm, "radius": 4 * mm});
            skCircle(sketch, "E80.3", {"center": v(60, -67.5) * mm, "radius": 4 * mm});
            skLineSegment(sketch, "E81.0", {"start": v(-80, -80) * mm, "end": v(-80, 80) * mm});
            skArc(sketch, "E81.1", {"start": v(-70, 90) * mm, "mid": v(-77.07, 87.07) * mm, "end": v(-80, 80) * mm});
            skLineSegment(sketch, "E81.2", {"start": v(-70, 90) * mm, "end": v(70, 90) * mm});
            skArc(sketch, "E81.3", {"start": v(80, 80) * mm, "mid": v(77.07, 87.07) * mm, "end": v(70, 90) * mm});
            skLineSegment(sketch, "E81.4", {"start": v(80, -80) * mm, "end": v(80, 80) * mm});
            skArc(sketch, "E81.5", {"start": v(70, -90) * mm, "mid": v(77.07, -87.07) * mm, "end": v(80, -80) * mm});
            skLineSegment(sketch, "E81.6", {"start": v(-70, -90) * mm, "end": v(70, -90) * mm});
            skArc(sketch, "E81.7", {"start": v(-80, -80) * mm, "mid": v(-77.07, -87.07) * mm, "end": v(-70, -90) * mm});
            skLineSegment(sketch, "E82", {"start": v(-29.12, 90) * mm, "end": v(-14.02, 108) * mm});
            skLineSegment(sketch, "E83", {"start": v(14.92, 108) * mm, "end": v(32.92, 90) * mm});
            skLineSegment(sketch, "E84", {"start": v(14.92, 116.05) * mm, "end": v(14.92, 108) * mm});
            skArc(sketch, "E85", {"start": v(14.92, 116.05) * mm, "mid": v(0.45, 135) * mm, "end": v(-14.02, 116.05) * mm});
            skCircle(sketch, "E86", {"center": v(0.45, 120) * mm, "radius": 6 * mm});
            skLineSegment(sketch, "E87", {"start": v(0.45, 120) * mm, "end": v(0.45, 90) * mm, "construction": true});
            skLineSegment(sketch, "E88", {"start": v(-14.02, 116.05) * mm, "end": v(-14.02, 108) * mm});
            skLineSegment(sketch, "E89.MirrorCS", {"start": v(0.45, -104.25) * mm, "end": v(0.45, -74.25) * mm, "construction": true});
            skLineSegment(sketch, "E90.MirrorCS", {"start": v(-29.12, -74.25) * mm, "end": v(-14.02, -92.25) * mm});
            skLineSegment(sketch, "E91.MirrorCS", {"start": v(14.92, -92.25) * mm, "end": v(32.92, -74.25) * mm});
            skLineSegment(sketch, "E92.MirrorCS", {"start": v(14.92, -100.3) * mm, "end": v(14.92, -92.25) * mm});
            skCircle(sketch, "E93.MirrorC", {"center": v(0.45, -104.25) * mm, "radius": 6 * mm});
            skArc(sketch, "E94.MirrorCS", {"start": v(14.92, -100.3) * mm, "mid": v(0.45, -119.25) * mm, "end": v(-14.02, -100.3) * mm});
            skLineSegment(sketch, "E95.MirrorCS", {"start": v(-14.02, -100.3) * mm, "end": v(-14.02, -92.25) * mm});
            skSolve(sketch);
        }
        {
            var Q0;
            Q0 = qSketchRegion(id + "F16", true);
            var Q1;
            Q1=makeQuery(id+"F2.opExtrude","CAP_FACE",FACE,{"disambiguationData":[OSD([sQuery(id+"F0.wireOp",EDGE,"E12"),sQuery(id+"F0.wireOp",EDGE,"E13"),sQuery(id+"F0.wireOp",EDGE,"E14"),sQuery(id+"F0.wireOp",EDGE,"E15"),sQuery(id+"F0.wireOp",EDGE,"E17.filletArc"),sQuery(id+"F0.wireOp",EDGE,"E18.filletArc"),sQuery(id+"F0.wireOp",EDGE,"E19.filletArc"),sQuery(id+"F0.wireOp",EDGE,"E20.filletArc"),sQuery(id+"F0.wireOp",EDGE,"E25.0"),sQuery(id+"F0.wireOp",EDGE,"E25.1"),sQuery(id+"F0.wireOp",EDGE,"E25.2"),sQuery(id+"F0.wireOp",EDGE,"E25.3"),sQuery(id+"F0.wireOp",EDGE,"E25.4"),sQuery(id+"F0.wireOp",EDGE,"E25.5"),sQuery(id+"F0.wireOp",EDGE,"E25.6"),sQuery(id+"F0.wireOp",EDGE,"E25.7")])],"isStart":false});
            extrude(context, id + "F17", {"entities" : qUnion([Q0]), "endBound" : BoundingType.UP_TO_SURFACE, "endBoundEntityFace" : qUnion([Q1]), "depth" : 25 * mm});
        }
    });
